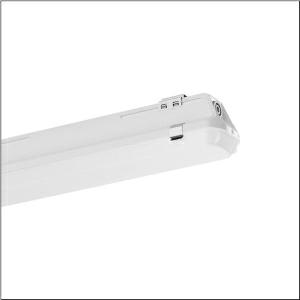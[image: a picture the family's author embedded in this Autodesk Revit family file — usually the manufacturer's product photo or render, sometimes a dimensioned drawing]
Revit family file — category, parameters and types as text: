
# Revit family: monsun_r__11_emergency_51fp20dp467h3h_e354
name_source: partatom
category: Lighting Fixtures
units: mm (PartAtom-declared; Revit-internal decimal feet)

## family parameters
Cut with Voids When Loaded = No
Host = Face
Light Source = No
Part Type = Normal
Room Calculation Point = No
Round Connector Dimension = Use Diameter
Shared = No

## types (1)
- --- (1 x LED, 790 lm, 5 W, 4000K)
    Apparent Load = 5 VA
    CIE Flux Codes = 45 75 93 94 100
    Color Rendering = 80
    Color Temperature = 4000K
    Default Elevation = 1800 mm
    Description = Monsun® 11 emergency, damp-proof luminaire, chain hanger, primary optical cover: enclosure, of PC, light emission: direct distribution, primary light characteristic: symmetric, installation type: suspended mounting, surface-mounted, horizontal mounting, vertical mounting, LED, rated luminous flux: 5.450lm, luminous efficacy: 158lm/W, light colour: 840, colour temperature: 4000K, control gear: ECG DALI, with terminal, 5+3-pole, max. 2.5mm², mains connection: 220..240V, AC, 50/60Hz, rated input power: 35W, control gear: single battery element, battery: NiCd, 4,5Ah, mains connection: 230V, luminaire housing, of glass-fibre reinforced polyester, uncoated, bright grey, incl. chain hanger, length: 1.590mm, width: 90mm, height: 88mm, clip for enclosure, of stainless steel (V2A), ceiling mounting element, of stainless steel (V2A), chain hanger, of stainless steel (V2A), protection rating (complete): IP66, insulation class (complete): insulation class I (protective earthing), certification: CE, UKCA, protection symbol: D, impact resistance: IK08, permissible operating ambient temperature: +5..+35°C, standard: EN 50419, EN 60598-2-1, EN 60598-2-22, no direct snow, no direct sun, no direct rain, for indoor or canopied outdoor use, corresponds to IFS (International Featured Standards) requirements for safety and quality in the food industry, contact your sales advisor before using the luminaires in applications with unclear chemical exposure, large temperature fluctuations or condensation-forming humidity, LABS conformity tested according to VDMA 24364:2018-05, packaging unit: 1 piece
    Height = 89 mm
    Lamp = 1 x LED
    Lamp Light Flux = 790 lm
    Lamp Power = 5 W
    Lamp count = 1
    Length = 1590 mm
    Luminous efficacy = 158 lm/W
    Manufacturer = Siteco
    ModVariant = No
    Model = 51FP20DP467H3H
    Mounting Place = Ceiling
    Mounting Type = Surface mounted
    Number of Poles = 1
    OnlyDefault = Yes
    Power Factor = 1
    Product Name = Monsun® 11 emergency
    Product group = damp-proof luminaire
    ProductGroupID = 300
    Protection Class = Protection class I
    Protection Degree = IP 66
    RLX_Detail_Level = 1
    RLX_Emergency_Light_Flux = 0 lm
    RLX_Emergency_Type = 0
    RLX_Emergency_Type_DB = No
    RlxData = <blob elided: 92657 chars, md5=84fc1be6>
    Socket = socket
    Standby Power = 0 W
    System Light Flux = 790 lm
    System Power = 5 W
    Type Comments = : emergency light operation: 3 h
    Type Image = l_1004748.jpg
    URL = http://relux.com
    VarID = @adj_134661
    Voltage = 0 V
    Weight = 0.00 kg
    Width = 90 mm

## geometry (parser evidence)
native form markers: Blend x4, Sweep x14
no freeform markers — native parametric forms only
